# Revit family: Grundplatten Typ III, zn
name_source: partatom
category: HLS-Bauteile
revit_build: Autodesk Revit 2017 (Build: 20190507_1515(x64)
units: mm (PartAtom-declared; Revit-internal decimal feet)

## family parameters
Arbeitsebenenbasiert = Ja
Beim Laden mit Abzugskörper schneiden = Nein
Bemaßung runder Anschluss = Durchmesser verwenden
Gemeinsam genutzt = Ja
Immer vertikal = Nein
Raumberechnungspunkt = Nein
Teiletyp = Normal

## types (2) — shared parameters
Abmessung = 137 x 70 x 8 mm
Anzahl Befestigungsloch = 2
B = 70 mm  [stored 0.229659 ft]
Breite = 70 mm  [stored 0.229659 ft]
D = 14 mm  [stored 0.0459318 ft]
Fabrikat = MEFA
Kurztext1 = Grundplatte Typ III ZnNi
L = 137 mm  [stored 0.449475 ft]
L1 = 95 mm
Langloch = 14x20 mm
Lochabstand längs = 95 mm
Lochdurchmesser = 14 mm
Länge = 137 mm  [stored 0.449475 ft]
MD = 8 mm  [stored 0.0262467 ft]
Material = Stahl
Materialname = S235
Mengeneinheit = St
Oberflaeche = Zink-Nickel
Stärke = 8 mm  [stored 0.0262467 ft]
Vorgabe-Ansicht = 1219 mm
max. zul. Last hängend = 10.00 kN
vpe = 1 St
zero-valued in all types: Sicherheitsfaktor

## per-type parameters (varying)
| type | Anschluss | Artikelnummer | EAN | Gewicht | Gewicht pro Bauteil | Gewindeanschluss | HGA | Kurztext2 |
| Grundplatte Typ III 137x70x8,0  1/2", zn | 1/2'' | 059060201/zn | 4250928456991 | 0.62 kg | 0.62 kg | Runde Gewindeanschlusse parametrik : Muffe 1/2´´ (0009865) | 15 mm  [stored 0.0492126 ft] | Anschluss 1/2'' Platte 137x70x8 mm |
| Grundplatte Typ III 137x70x8,0  1", zn | 1'' | 059060001/zn | 4250928457004 | 0.67 kg | 0.67 kg | Runde Gewindeanschlusse parametrik : Muffe 1´´ (0009881) | 20 mm  [stored 0.0656168 ft] | Anschluss 1'' Platte 137x70x8 mm |

note: [stored X ft] marks values corroborated as IEEE doubles in the binary element streams (Revit-internal decimal feet)

## geometry (parser evidence)
native form markers: Sweep x7
no freeform markers — native parametric forms only
